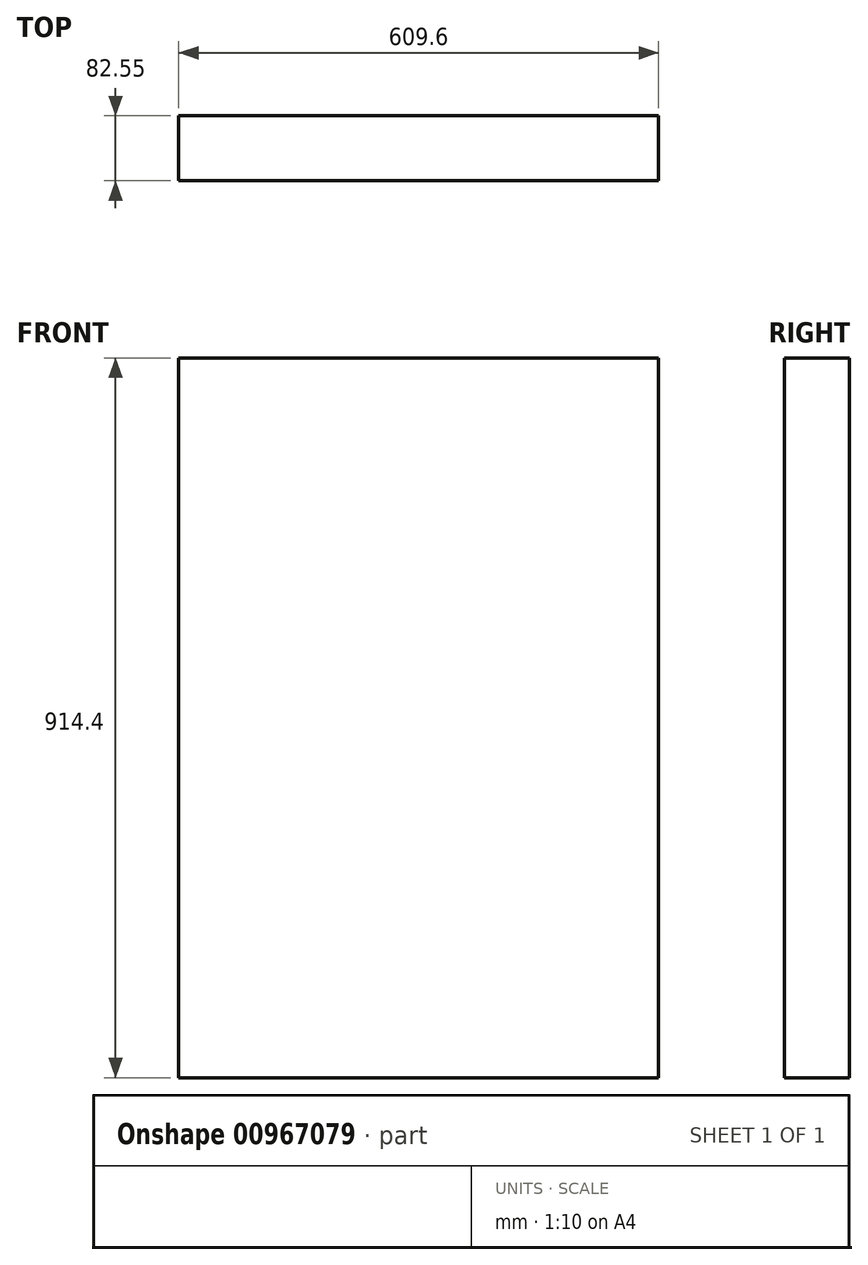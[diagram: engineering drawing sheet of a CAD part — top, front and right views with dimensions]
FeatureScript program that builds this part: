
annotation { "Feature Type Name" : "Feature", "Feature Type Description" : "" }
export const myFeature = defineFeature(function(context is Context, id is Id, definition is map)
    precondition{}
    {
        {
            var Q0;
            Q0=qCreatedBy(makeId("Front.planeOp"),FACE);
            var sketch = newSketch(context, id + "F0", { "sketchPlane" : qUnion([Q0])});
            skLineSegment(sketch, "E0.bottom", {"start": v(0, 0) * mm, "end": v(-609.6, 0) * mm});
            skLineSegment(sketch, "E0.top", {"start": v(0, 914.4) * mm, "end": v(-609.6, 914.4) * mm});
            skLineSegment(sketch, "E0.left", {"start": v(0, 0) * mm, "end": v(0, 914.4) * mm});
            skLineSegment(sketch, "E0.right", {"start": v(-609.6, 0) * mm, "end": v(-609.6, 914.4) * mm});
            skSolve(sketch);
        }
        {
            var Q0;
            Q0 = qSketchRegion(id + "F0", true);
            extrude(context, id + "F1", {"entities" : qUnion([Q0]), "oppositeDirection" : true, "depth" : 82.55 * mm, "offsetDistance" : 25.4 * mm});
        }
    });
